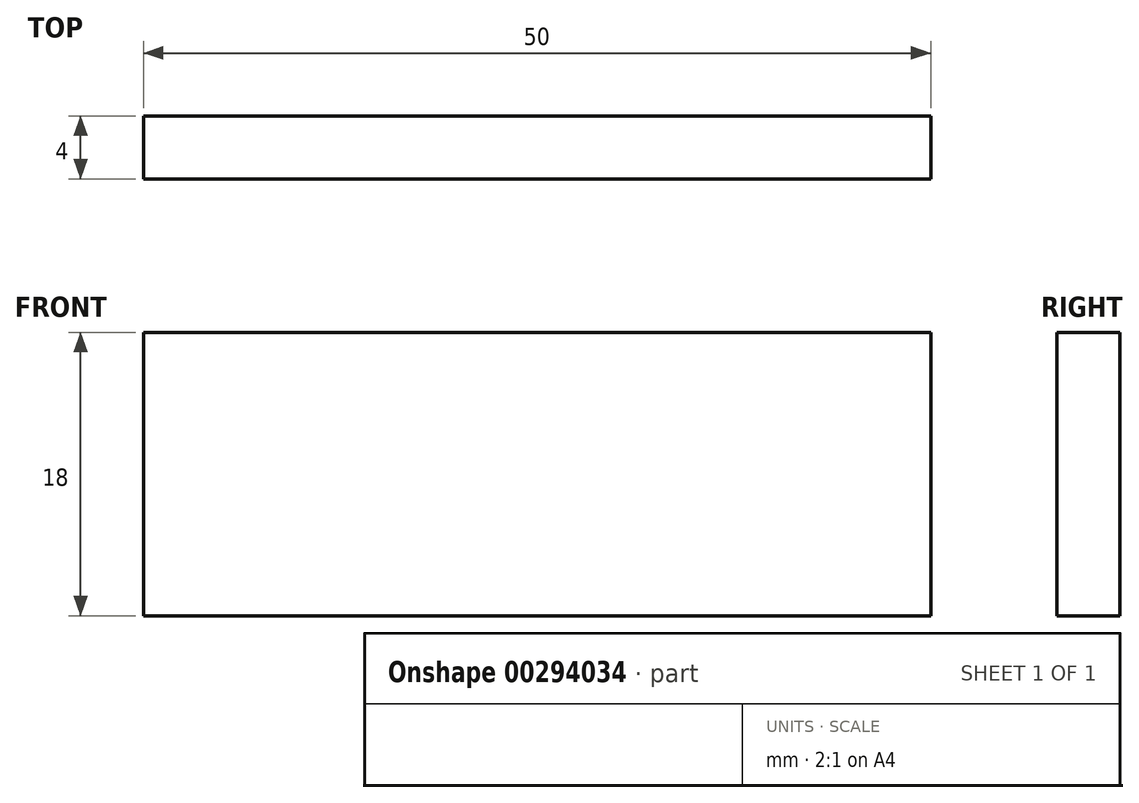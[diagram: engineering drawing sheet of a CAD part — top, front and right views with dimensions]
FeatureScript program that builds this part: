
annotation { "Feature Type Name" : "Feature", "Feature Type Description" : "" }
export const myFeature = defineFeature(function(context is Context, id is Id, definition is map)
    precondition{}
    {
        {
            var Q0;
            Q0=qCreatedBy(makeId("Front.planeOp"),FACE);
            var sketch = newSketch(context, id + "F0", { "sketchPlane" : qUnion([Q0])});
            skLineSegment(sketch, "E0.bottom", {"start": v(25, 9) * mm, "end": v(-25, 9) * mm});
            skLineSegment(sketch, "E0.top", {"start": v(25, -9) * mm, "end": v(-25, -9) * mm});
            skLineSegment(sketch, "E0.left", {"start": v(25, 9) * mm, "end": v(25, -9) * mm});
            skLineSegment(sketch, "E0.right", {"start": v(-25, 9) * mm, "end": v(-25, -9) * mm});
            skPoint(sketch, "E0.middle", {"position": v(0, 0) * mm});
            skSolve(sketch);
        }
        {
            var Q0;
            Q0=makeQuery(id+"F0.imprint","IMPRINT",FACE,{"disambiguationData":[TD([[makeQuery(id+"F0.imprint","IMPRINT",EDGE,{"derivedFrom":sQuery(id+"F0.wireOp",EDGE,"E0.bottom")}),1.0]])]});
            extrude(context, id + "F1", {"entities" : qUnion([Q0]), "depth" : 4 * mm});
        }
    });
